# Revit family: Soap Dispenser_Metlam_Rectangular_Vertical_Button Pump
name_source: partatom
category: Specialty Equipment
revit_build: Autodesk Revit 2016 (Build: 20170117_1200(x64)
units: mm (PartAtom-declared; Revit-internal decimal feet)

## family parameters
Always vertical = Yes
Cut with Voids When Loaded = No
OmniClass Number = 23.40.20.21.34
OmniClass Title = Soap Holders, Dispensers
Part Type = Normal
Room Calculation Point = Yes
Round Connector Dimension = Use Diameter
Shared = No
Work Plane-Based = No

## types (1)
- 123w x 93d x 209h (ML605BS)
    Button_Material = z_Metlam_Black
    Description = Vertical Soap Dispenser - SS button pump valve
    Indicator_Material = z_Metlam_Plastic_Clear Gray
    Manufacturer = Metlam
    Manufacturer_Overall Depth = 93 mm
    Manufacturer_Overall Height = 209 mm
    Manufacturer_Overall Width = 123 mm
    Manufacturer_Spec Code = ML605BS
    Manufacturer_URL__Product Specific = http://www.metlam.com.au
    Material_ANZRS = z_Metlam_Metal_Stainless Steel_Satin
    Model = ML605BS
    Type Comments = Soap Dispensers
    URL = http://www.metlam.com.au

## geometry (parser evidence)
native form markers: Sweep x2
no freeform markers — native parametric forms only
